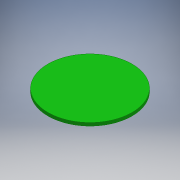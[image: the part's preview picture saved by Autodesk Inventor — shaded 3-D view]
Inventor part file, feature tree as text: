
AUTODESK INVENTOR PART (.ipt)
format: ipt  version: 2018.3 (Build 223284000, 284)  size: 93,184 bytes
history: native  units: mm
features: extrude x1, sketch x1
ambient origin geometry x8: Origin, YZ Plane, XZ Plane, XY Plane, X Axis, Y Axis, Z Axis, Center Point
bodies: Solid1 (feature_tree)
feature tree (2):
  extrude  "Extrusion1"  Depth=1.0mm TaperAngle=0.0deg
  sketch  "Sketch1"  dims[d0=27.0mm d1=1.0mm d2=0.0mm]
